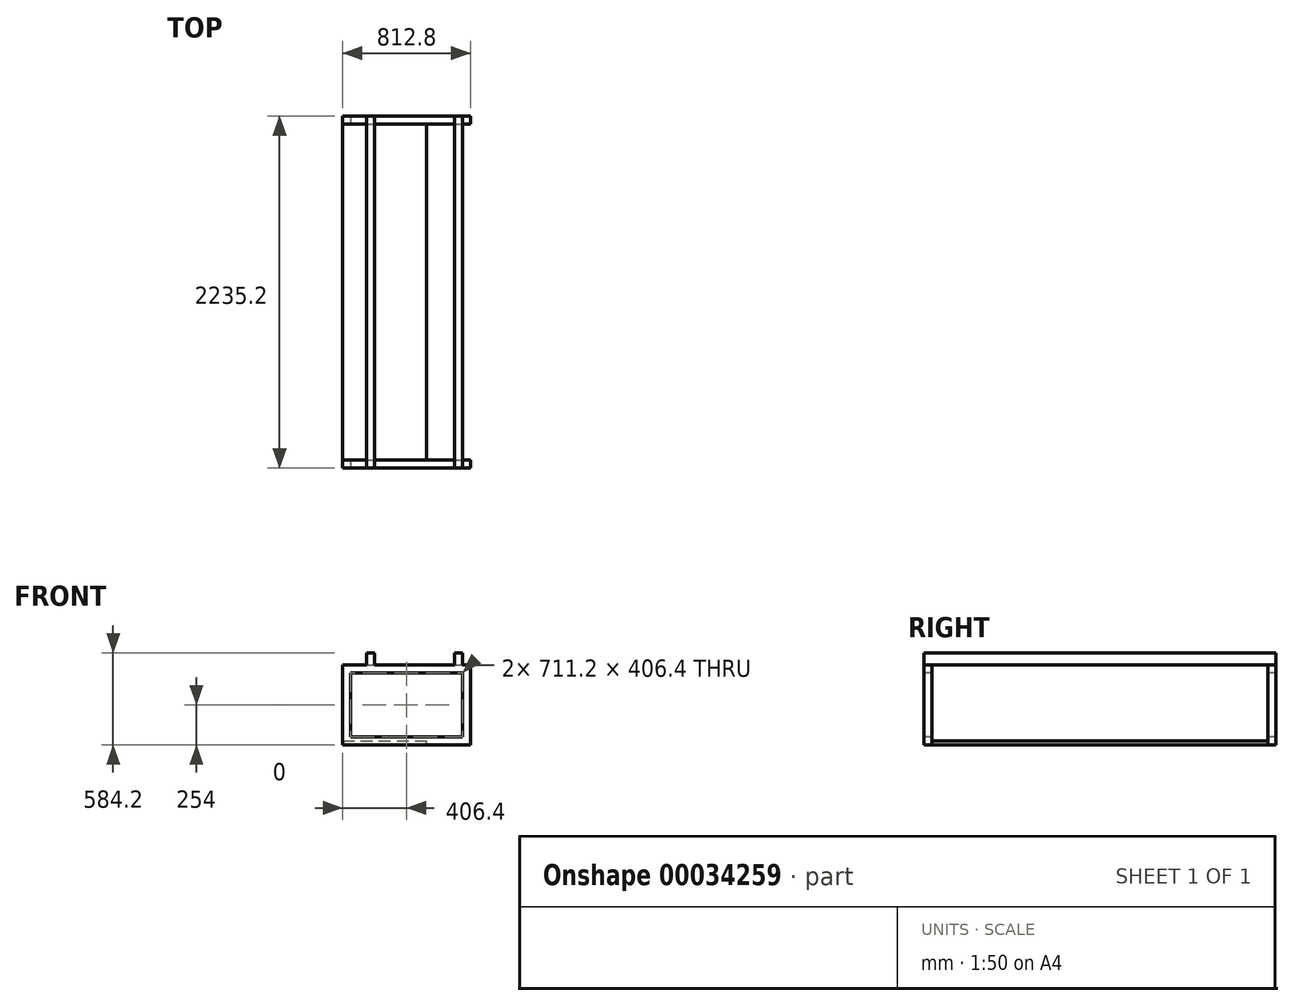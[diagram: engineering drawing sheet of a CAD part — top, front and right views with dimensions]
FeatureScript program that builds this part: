
annotation { "Feature Type Name" : "Feature", "Feature Type Description" : "" }
export const myFeature = defineFeature(function(context is Context, id is Id, definition is map)
    precondition{}
    {
        {
            var Q0;
            Q0=qCreatedBy(makeId("Front.planeOp"),FACE);
            var sketch = newSketch(context, id + "F0", { "sketchPlane" : qUnion([Q0])});
            skLineSegment(sketch, "E0.bottom", {"start": v(0, 0) * mm, "end": v(-812.8, 0) * mm});
            skLineSegment(sketch, "E0.top", {"start": v(0, 584.2) * mm, "end": v(-812.8, 584.2) * mm});
            skLineSegment(sketch, "E0.left", {"start": v(0, 0) * mm, "end": v(0, 584.2) * mm});
            skLineSegment(sketch, "E0.right", {"start": v(-812.8, 0) * mm, "end": v(-812.8, 584.2) * mm});
            skSolve(sketch);
        }
        {
            var Q0;
            Q0=makeQuery(id+"F0.imprint","IMPRINT",FACE,{"disambiguationData":[TD([[makeQuery(id+"F0.imprint","IMPRINT",EDGE,{"derivedFrom":sQuery(id+"F0.wireOp",EDGE,"E0.bottom")}),-1.0]])]});
            extrude(context, id + "F1", {"entities" : qUnion([Q0]), "depth" : 2235.2 * mm});
        }
        {
            var Q0;
            Q0=makeQuery(id+"F1.opExtrude","CAP_FACE",FACE,{"disambiguationData":[OSD([sQuery(id+"F0.wireOp",EDGE,"E0.bottom"),sQuery(id+"F0.wireOp",EDGE,"E0.top"),sQuery(id+"F0.wireOp",EDGE,"E0.left"),sQuery(id+"F0.wireOp",EDGE,"E0.right")])],"isStart":false});
            var sketch = newSketch(context, id + "F2", { "sketchPlane" : qUnion([Q0])});
            skLineSegment(sketch, "E1.bottom", {"start": v(-812.8, 584.2) * mm, "end": v(-660.4, 584.2) * mm});
            skLineSegment(sketch, "E1.top", {"start": v(-812.8, 508) * mm, "end": v(-660.4, 508) * mm});
            skLineSegment(sketch, "E1.left", {"start": v(-812.8, 584.2) * mm, "end": v(-812.8, 508) * mm});
            skLineSegment(sketch, "E1.right", {"start": v(-660.4, 584.2) * mm, "end": v(-660.4, 508) * mm});
            skLineSegment(sketch, "E2.bottom", {"start": v(-609.6, 584.2) * mm, "end": v(-101.6, 584.2) * mm});
            skLineSegment(sketch, "E2.top", {"start": v(-609.6, 508) * mm, "end": v(-101.6, 508) * mm});
            skLineSegment(sketch, "E2.left", {"start": v(-609.6, 584.2) * mm, "end": v(-609.6, 508) * mm});
            skLineSegment(sketch, "E2.right", {"start": v(-101.6, 584.2) * mm, "end": v(-101.6, 508) * mm});
            skLineSegment(sketch, "E3.bottom", {"start": v(-50.8, 584.2) * mm, "end": v(0, 584.2) * mm});
            skLineSegment(sketch, "E3.top", {"start": v(-50.8, 508) * mm, "end": v(0, 508) * mm});
            skLineSegment(sketch, "E3.left", {"start": v(-50.8, 584.2) * mm, "end": v(-50.8, 508) * mm});
            skLineSegment(sketch, "E3.right", {"start": v(0, 584.2) * mm, "end": v(0, 508) * mm});
            skSolve(sketch);
        }
        {
            var Q0;
            Q0=makeQuery(id+"F2.imprint","IMPRINT",FACE,{"disambiguationData":[TD([[makeQuery(id+"F2.imprint","IMPRINT",EDGE,{"derivedFrom":sQuery(id+"F2.wireOp",EDGE,"E1.bottom")}),1.0]])]});
            var Q1;
            Q1=makeQuery(id+"F2.imprint","IMPRINT",FACE,{"disambiguationData":[TD([[makeQuery(id+"F2.imprint","IMPRINT",EDGE,{"derivedFrom":sQuery(id+"F2.wireOp",EDGE,"E2.bottom")}),1.0]])]});
            var Q2;
            Q2=makeQuery(id+"F2.imprint","IMPRINT",FACE,{"disambiguationData":[TD([[makeQuery(id+"F2.imprint","IMPRINT",EDGE,{"derivedFrom":sQuery(id+"F2.wireOp",EDGE,"E3.bottom")}),1.0]])]});
            extrude(context, id + "F3", {"entities" : qUnion([Q0, Q1, Q2]), "operationType" : NewBodyOperationType.REMOVE, "endBound" : BoundingType.THROUGH_ALL, "oppositeDirection" : true, "depth" : 25.4 * mm});
        }
        {
            var Q0;
            Q0=makeQuery(id+"F1.opExtrude","CAP_FACE",FACE,{"disambiguationData":[OSD([sQuery(id+"F0.wireOp",EDGE,"E0.bottom"),sQuery(id+"F0.wireOp",EDGE,"E0.top"),sQuery(id+"F0.wireOp",EDGE,"E0.left"),sQuery(id+"F0.wireOp",EDGE,"E0.right")])],"isStart":false});
            var sketch = newSketch(context, id + "F4", { "sketchPlane" : qUnion([Q0])});
            skLineSegment(sketch, "E4.bottom", {"start": v(-762, 457.2) * mm, "end": v(-50.8, 457.2) * mm});
            skLineSegment(sketch, "E4.top", {"start": v(-762, 50.8) * mm, "end": v(-50.8, 50.8) * mm});
            skLineSegment(sketch, "E4.left", {"start": v(-762, 457.2) * mm, "end": v(-762, 50.8) * mm});
            skLineSegment(sketch, "E4.right", {"start": v(-50.8, 457.2) * mm, "end": v(-50.8, 50.8) * mm});
            skSolve(sketch);
        }
        {
            var Q0;
            Q0=makeQuery(id+"F4.imprint","IMPRINT",FACE,{"disambiguationData":[TD([[makeQuery(id+"F4.imprint","IMPRINT",EDGE,{"derivedFrom":sQuery(id+"F4.wireOp",EDGE,"E4.bottom")}),-1.0]])]});
            extrude(context, id + "F5", {"entities" : qUnion([Q0]), "operationType" : NewBodyOperationType.REMOVE, "endBound" : BoundingType.THROUGH_ALL, "oppositeDirection" : true, "depth" : 25.4 * mm});
        }
        {
            var Q0;
            Q0=makeQuery(id+"F1.opExtrude","SWEPT_FACE",FACE,{"disambiguationData":[OSD([sQuery(id+"F0.wireOp",EDGE,"E0.left")])]});
            var sketch = newSketch(context, id + "F6", { "sketchPlane" : qUnion([Q0])});
            skLineSegment(sketch, "E5.bottom", {"start": v(-2184.4, 508) * mm, "end": v(-50.8, 508) * mm});
            skLineSegment(sketch, "E5.top", {"start": v(-2184.4, 25.4) * mm, "end": v(-50.8, 25.4) * mm});
            skLineSegment(sketch, "E5.left", {"start": v(-2184.4, 508) * mm, "end": v(-2184.4, 25.4) * mm});
            skLineSegment(sketch, "E5.right", {"start": v(-50.8, 508) * mm, "end": v(-50.8, 25.4) * mm});
            skSolve(sketch);
        }
        {
            var Q0;
            Q0=makeQuery(id+"F6.imprint","IMPRINT",FACE,{"disambiguationData":[TD([[makeQuery(id+"F6.imprint","IMPRINT",EDGE,{"derivedFrom":sQuery(id+"F6.wireOp",EDGE,"E5.bottom")}),1.0]])]});
            extrude(context, id + "F7", {"entities" : qUnion([Q0]), "operationType" : NewBodyOperationType.REMOVE, "endBound" : BoundingType.THROUGH_ALL, "oppositeDirection" : true, "depth" : 25.4 * mm});
        }
        {
            var Q0;
            Q0=makeQuery(id+"F7.boolean.opBoolean","COPY",FACE,{"derivedFrom":makeQuery(id+"F7.opExtrude","SWEPT_FACE",FACE,{"disambiguationData":[OSD([sQuery(id+"F6.wireOp",EDGE,"E5.top")])]})});
            var sketch = newSketch(context, id + "F8", { "sketchPlane" : qUnion([Q0])});
            skLineSegment(sketch, "E6.bottom", {"start": v(0, -50.8) * mm, "end": v(-279.4, -50.8) * mm});
            skLineSegment(sketch, "E6.top", {"start": v(0, -2184.4) * mm, "end": v(-279.4, -2184.4) * mm});
            skLineSegment(sketch, "E6.left", {"start": v(0, -50.8) * mm, "end": v(0, -2184.4) * mm});
            skLineSegment(sketch, "E6.right", {"start": v(-279.4, -50.8) * mm, "end": v(-279.4, -2184.4) * mm});
            skSolve(sketch);
        }
        {
            var Q0;
            Q0=makeQuery(id+"F8.imprint","IMPRINT",FACE,{"disambiguationData":[TD([[makeQuery(id+"F8.imprint","IMPRINT",EDGE,{"derivedFrom":sQuery(id+"F8.wireOp",EDGE,"E6.bottom")}),-1.0]])]});
            extrude(context, id + "F9", {"entities" : qUnion([Q0]), "operationType" : NewBodyOperationType.REMOVE, "oppositeDirection" : true, "depth" : 25.4 * mm});
        }
    });
